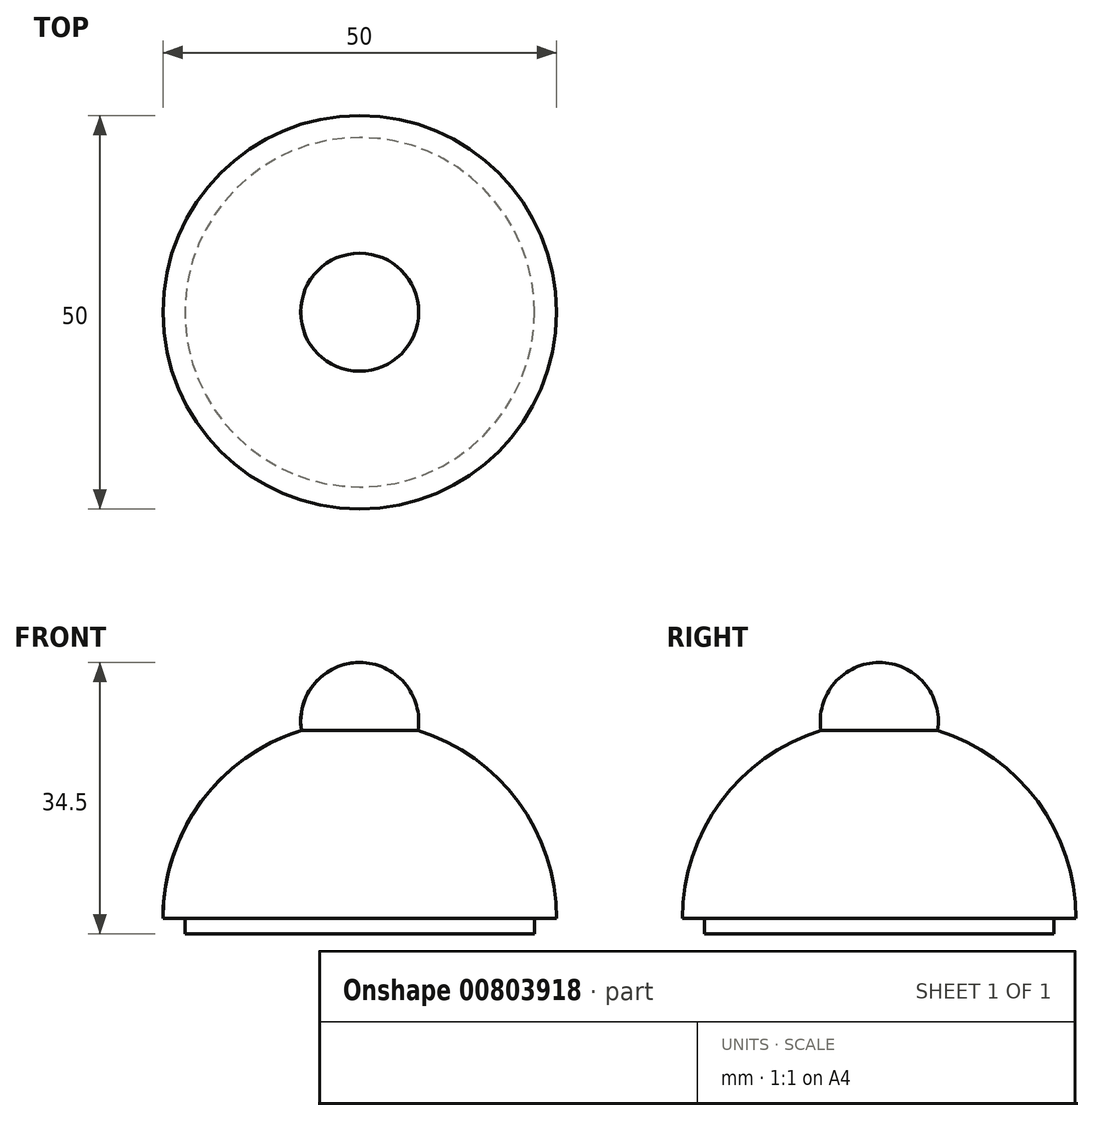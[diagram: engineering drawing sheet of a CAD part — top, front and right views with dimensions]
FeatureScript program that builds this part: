
annotation { "Feature Type Name" : "Feature", "Feature Type Description" : "" }
export const myFeature = defineFeature(function(context is Context, id is Id, definition is map)
    precondition{}
    {
        {
            var Q0;
            Q0=qCreatedBy(makeId("Front.planeOp"),FACE);
            var sketch = newSketch(context, id + "F0", { "sketchPlane" : qUnion([Q0])});
            skArc(sketch, "E0", {"start": v(-7.42, 23.88) * mm, "mid": v(-20.13, 14.83) * mm, "end": v(-25, 0) * mm});
            skLineSegment(sketch, "E1", {"start": v(-25, 0) * mm, "end": v(-22.2, 0) * mm});
            skLineSegment(sketch, "E2", {"start": v(0, 0) * mm, "end": v(0, 25) * mm});
            skLineSegment(sketch, "E3.top", {"start": v(0, -2) * mm, "end": v(-22.2, -2) * mm});
            skLineSegment(sketch, "E3.left", {"start": v(0, 0) * mm, "end": v(0, -2) * mm});
            skLineSegment(sketch, "E3.right", {"start": v(-22.2, 0) * mm, "end": v(-22.2, -2) * mm});
            skArc(sketch, "E4", {"start": v(0, 32.5) * mm, "mid": v(-5.69, 29.89) * mm, "end": v(-7.42, 23.88) * mm});
            skLineSegment(sketch, "E5", {"start": v(0, 25) * mm, "end": v(0, 32.5) * mm});
            skSolve(sketch);
        }
        {
            var Q0;
            Q0=makeQuery(id+"F0.imprint","IMPRINT",FACE,{"disambiguationData":[TD([[makeQuery(id+"F0.imprint","IMPRINT",EDGE,{"derivedFrom":sQuery(id+"F0.wireOp",EDGE,"E0")}),1.0]])]});
            var Q1;
            Q1=sQuery(id+"F0.wireOp",EDGE,"E2");
            revolve(context, id + "F1", {"surfaceOperationType" : NewSurfaceOperationType.NEW, "entities" : qUnion([Q0]), "axis" : qUnion([Q1]), "revolveType" : RevolveType.FULL});
        }
    });
